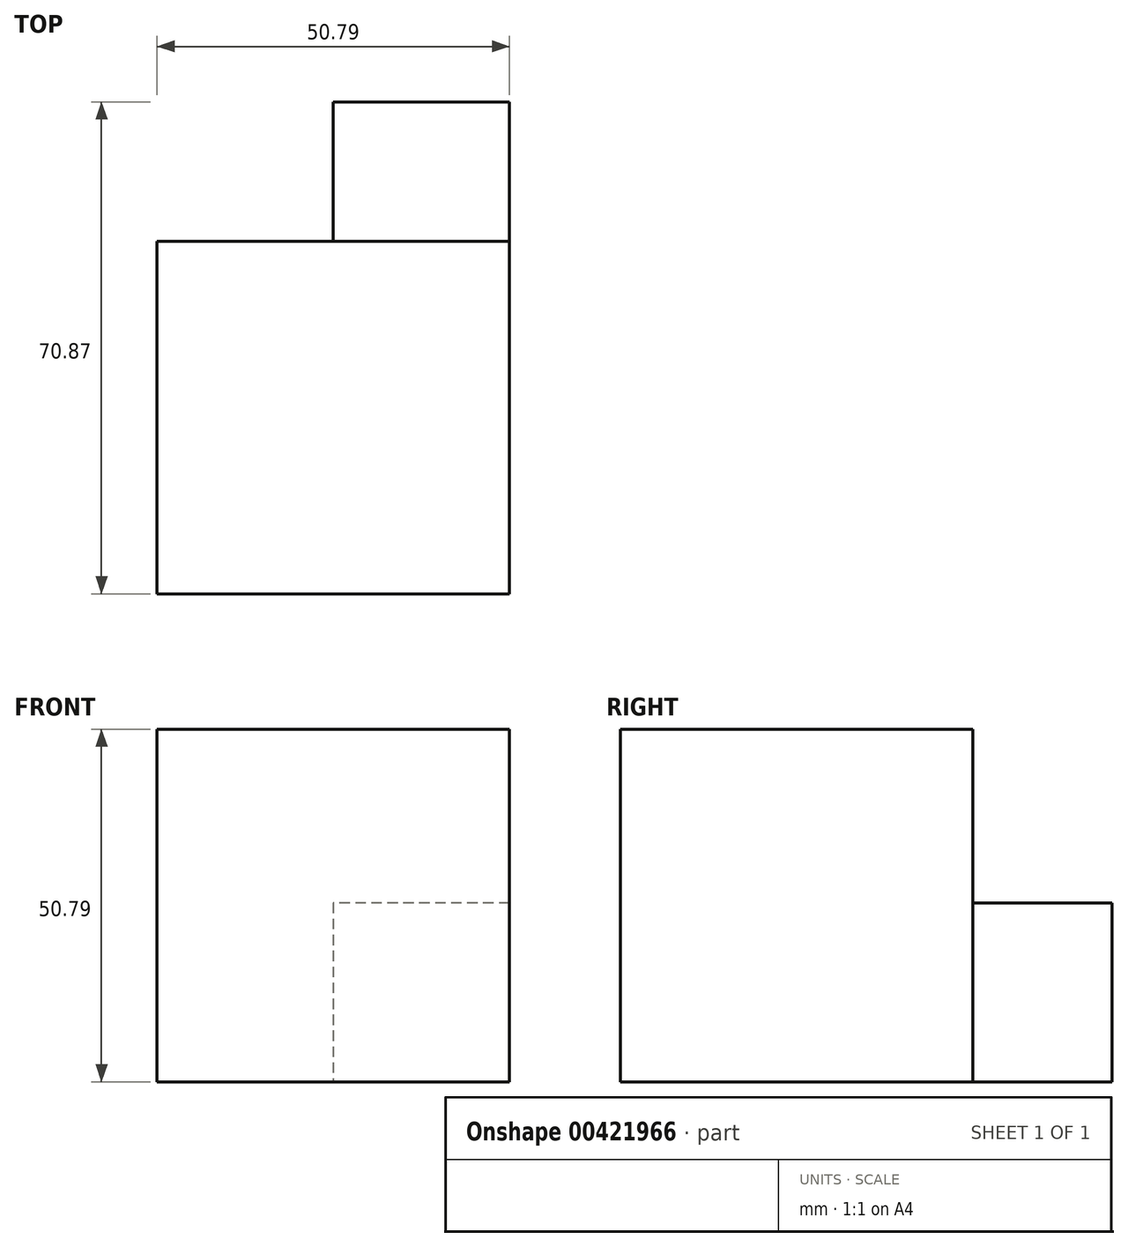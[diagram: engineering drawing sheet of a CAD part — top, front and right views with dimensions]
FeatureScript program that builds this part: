
annotation { "Feature Type Name" : "Feature", "Feature Type Description" : "" }
export const myFeature = defineFeature(function(context is Context, id is Id, definition is map)
    precondition{}
    {
        {
            var Q0;
            Q0=qCreatedBy(makeId("Front.planeOp"),FACE);
            var sketch = newSketch(context, id + "F0", { "sketchPlane" : qUnion([Q0])});
            skLineSegment(sketch, "E0", {"start": v(0, 0) * mm, "end": v(0, 50.8) * mm});
            skLineSegment(sketch, "E1", {"start": v(0, 50.8) * mm, "end": v(-50.8, 50.8) * mm});
            skLineSegment(sketch, "E2", {"start": v(-50.8, 50.8) * mm, "end": v(-50.8, 0) * mm});
            skLineSegment(sketch, "E3", {"start": v(-50.8, 0) * mm, "end": v(0, 0) * mm});
            skSolve(sketch);
        }
        {
            var Q0;
            Q0=makeQuery(id+"F0.imprint","IMPRINT",FACE,{"disambiguationData":[TD([[makeQuery(id+"F0.imprint","IMPRINT",EDGE,{"derivedFrom":sQuery(id+"F0.wireOp",EDGE,"E0")}),1.0]])]});
            extrude(context, id + "F1", {"entities" : qUnion([Q0]), "depth" : 50.8 * mm});
        }
        {
            var Q0;
            Q0=qCreatedBy(makeId("Front.planeOp"),FACE);
            var sketch = newSketch(context, id + "F2", { "sketchPlane" : qUnion([Q0])});
            skLineSegment(sketch, "E4", {"start": v(-50.8, 0) * mm, "end": v(-50.8, 25.4) * mm});
            skLineSegment(sketch, "E5", {"start": v(-50.8, 25.4) * mm, "end": v(-25.4, 25.4) * mm});
            skLineSegment(sketch, "E6", {"start": v(-25.4, 25.4) * mm, "end": v(-25.4, 0) * mm});
            skLineSegment(sketch, "E7", {"start": v(-25.4, 0) * mm, "end": v(-50.8, 0) * mm});
            skSolve(sketch);
        }
        {
            var Q0;
            Q0 = qSketchRegion(id + "F2", true);
            extrude(context, id + "F3", {"entities" : qUnion([Q0]), "operationType" : NewBodyOperationType.ADD, "depth" : 25.4 * mm});
        }
        {
            var Q0;
            Q0=qCreatedBy(makeId("Front.planeOp"),FACE);
            var sketch = newSketch(context, id + "F4", { "sketchPlane" : qUnion([Q0])});
            skLineSegment(sketch, "E8", {"start": v(0, 0) * mm, "end": v(-25.4, 0) * mm});
            skLineSegment(sketch, "E9", {"start": v(-25.4, 0) * mm, "end": v(-25.4, 25.4) * mm});
            skLineSegment(sketch, "E10", {"start": v(-25.4, 25.4) * mm, "end": v(0, 25.4) * mm});
            skLineSegment(sketch, "E11", {"start": v(0, 25.4) * mm, "end": v(0, 0) * mm});
            skSolve(sketch);
        }
        {
            var Q0;
            Q0=makeQuery(id+"F4.imprint","IMPRINT",FACE,{"disambiguationData":[TD([[makeQuery(id+"F4.imprint","IMPRINT",EDGE,{"derivedFrom":sQuery(id+"F4.wireOp",EDGE,"E8")}),-1.0]])]});
            var Q1;
            Q1=sQuery(id+"F4.wireOp",EDGE,"E10");
            extrude(context, id + "F5", {"entities" : qUnion([Q0]), "bodyType" : ToolBodyType.SURFACE, "operationType" : NewBodyOperationType.ADD, "surfaceEntities" : qUnion([Q1]), "depth" : 25.4 * mm});
        }
        {
            var Q0;
            Q0=qCreatedBy(makeId("Front.planeOp"),FACE);
            var sketch = newSketch(context, id + "F6", { "sketchPlane" : qUnion([Q0])});
            skLineSegment(sketch, "E12", {"start": v(0, 25.78) * mm, "end": v(-25.4, 25.78) * mm});
            skLineSegment(sketch, "E13", {"start": v(-25.4, 25.78) * mm, "end": v(-25.4, 0) * mm});
            skLineSegment(sketch, "E14", {"start": v(-25.4, 0) * mm, "end": v(0, 0) * mm});
            skLineSegment(sketch, "E15", {"start": v(0, 0) * mm, "end": v(0, 25.78) * mm});
            skSolve(sketch);
        }
        {
            var Q0;
            Q0=makeQuery(id+"F6.imprint","IMPRINT",FACE,{"disambiguationData":[TD([[makeQuery(id+"F6.imprint","IMPRINT",EDGE,{"derivedFrom":sQuery(id+"F6.wireOp",EDGE,"E12")}),1.0]])]});
            extrude(context, id + "F7", {"entities" : qUnion([Q0]), "oppositeDirection" : true, "depth" : 20.07 * mm});
        }
    });
